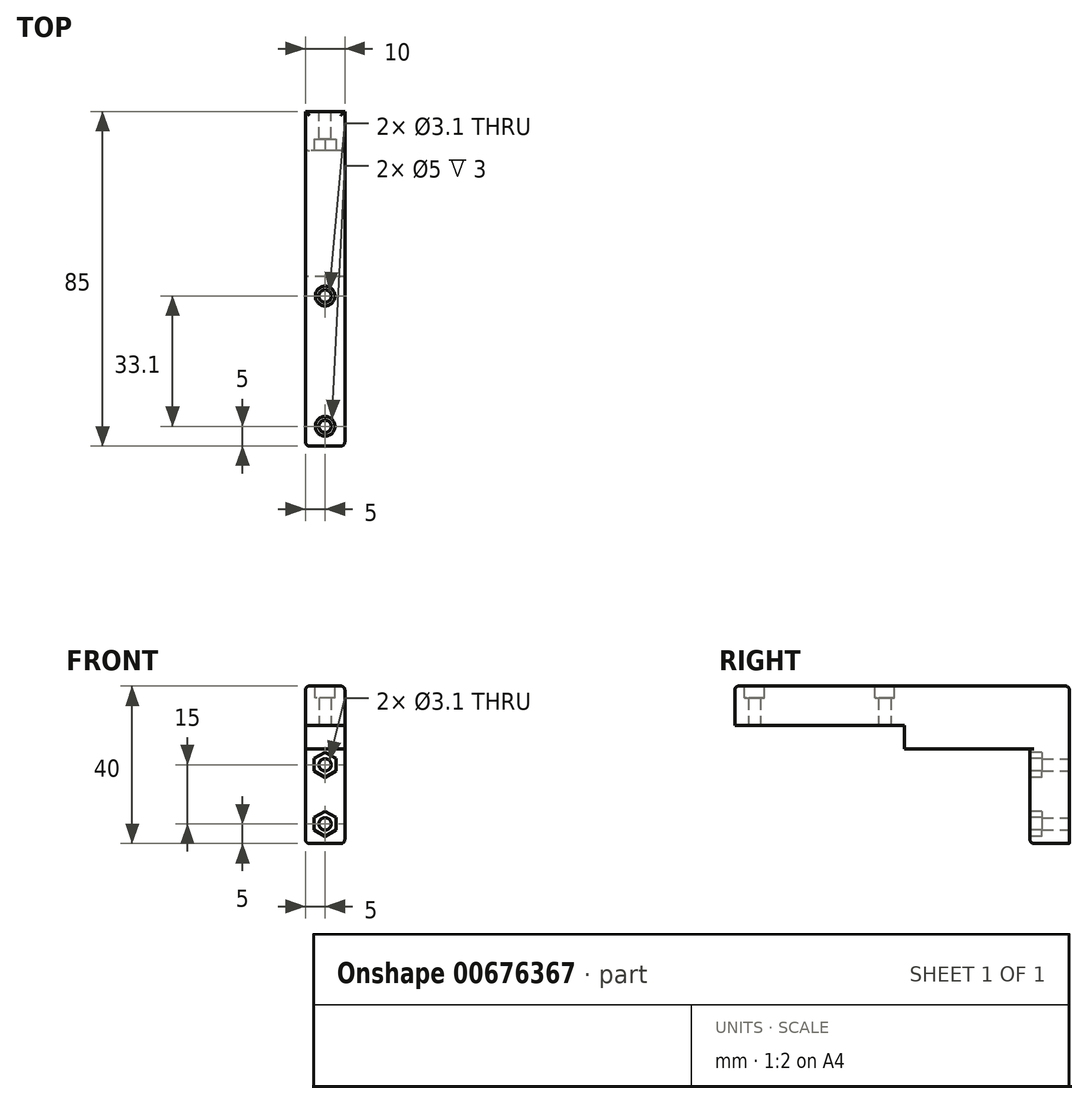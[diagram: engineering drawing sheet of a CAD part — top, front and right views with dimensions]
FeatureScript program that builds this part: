
annotation { "Feature Type Name" : "Feature", "Feature Type Description" : "" }
export const myFeature = defineFeature(function(context is Context, id is Id, definition is map)
    precondition{}
    {
        {
            var Q0;
            Q0=qCreatedBy(makeId("Top.planeOp"),FACE);
            var sketch = newSketch(context, id + "F0", { "sketchPlane" : qUnion([Q0])});
            skLineSegment(sketch, "E0.bottom", {"start": v(0, 0) * mm, "end": v(-10, 0) * mm});
            skLineSegment(sketch, "E0.top", {"start": v(0, 85) * mm, "end": v(-10, 85) * mm});
            skLineSegment(sketch, "E0.left", {"start": v(0, 0) * mm, "end": v(0, 85) * mm});
            skLineSegment(sketch, "E0.right", {"start": v(-10, 0) * mm, "end": v(-10, 85) * mm});
            skCircle(sketch, "E1", {"center": v(-5, 5) * mm, "radius": 1.55 * mm});
            skPoint(sketch, "E1.centerSnap0", {"position": v(-5, 0) * mm});
            skCircle(sketch, "E2", {"center": v(-5, 38.1) * mm, "radius": 1.55 * mm});
            skLineSegment(sketch, "E3", {"start": v(0, 43.1) * mm, "end": v(-10, 43.1) * mm});
            skLineSegment(sketch, "E4", {"start": v(0, 75) * mm, "end": v(-10, 75) * mm});
            skSolve(sketch);
        }
        {
            var Q0;
            {var subQ1=sQuery(id+"F0.wireOp",EDGE,"E0.bottom");Q0=makeQuery(id+"F0.imprint","IMPRINT",FACE,{"disambiguationData":[TD([[makeQuery(id+"F0.imprint","IMPRINT",EDGE,{"derivedFrom":subQ1}),-1.0]])]});}
            extrude(context, id + "F1", {"entities" : qUnion([Q0]), "depth" : 10 * mm, "offsetDistance" : 25 * mm});
        }
        {
            var Q0;
            {var subQ0=sQuery(id+"F0.wireOp",EDGE,"E3");Q0=makeQuery(id+"F0.imprint","IMPRINT",FACE,{"disambiguationData":[TD([[makeQuery(id+"F0.imprint","IMPRINT",EDGE,{"derivedFrom":subQ0}),-1.0]])]});}
            extrude(context, id + "F2", {"entities" : qUnion([Q0]), "operationType" : NewBodyOperationType.ADD, "depth" : 10 * mm, "offsetDistance" : 25 * mm, "hasSecondDirection" : true, "secondDirectionOppositeDirection" : true, "secondDirectionDepth" : 6 * mm});
        }
        {
            var Q0;
            {var subQ0=sQuery(id+"F0.wireOp",EDGE,"E0.top");Q0=makeQuery(id+"F0.imprint","IMPRINT",FACE,{"disambiguationData":[TD([[makeQuery(id+"F0.imprint","IMPRINT",EDGE,{"derivedFrom":subQ0}),1.0]])]});}
            extrude(context, id + "F3", {"entities" : qUnion([Q0]), "operationType" : NewBodyOperationType.ADD, "oppositeDirection" : true, "depth" : 30 * mm, "offsetDistance" : 25 * mm, "hasSecondDirection" : true, "secondDirectionOppositeDirection" : false, "secondDirectionDepth" : 10 * mm});
        }
        {
            var Q0;
            Q0=makeQuery(id+"F3.opExtrude","SWEPT_FACE",FACE,{"disambiguationData":[OSD([sQuery(id+"F0.wireOp",EDGE,"E0.top")])]});
            var sketch = newSketch(context, id + "F4", { "sketchPlane" : qUnion([Q0])});
            skCircle(sketch, "E5", {"center": v(5, -10) * mm, "radius": 1.55 * mm});
            skPoint(sketch, "E5.centerSnap0", {"position": v(5, 10) * mm});
            skPoint(sketch, "E5.perimeterSnap0", {"position": v(0, -10) * mm});
            skCircle(sketch, "E6", {"center": v(5, -25) * mm, "radius": 1.55 * mm});
            skSolve(sketch);
        }
        {
            var Q0;
            Q0=makeQuery(id+"F4.imprint","IMPRINT",FACE,{"disambiguationData":[TD([[makeQuery(id+"F4.imprint","IMPRINT",EDGE,{"derivedFrom":sQuery(id+"F4.wireOp",EDGE,"E6")}),1.0]])]});
            var Q1;
            Q1=makeQuery(id+"F4.imprint","IMPRINT",FACE,{"disambiguationData":[TD([[makeQuery(id+"F4.imprint","IMPRINT",EDGE,{"derivedFrom":sQuery(id+"F4.wireOp",EDGE,"E5")}),1.0]])]});
            extrude(context, id + "F5", {"entities" : qUnion([Q0, Q1]), "operationType" : NewBodyOperationType.REMOVE, "oppositeDirection" : true, "depth" : 15 * mm, "offsetDistance" : 25 * mm});
        }
        {
            var Q0;
            {var subQ0=sQuery(id+"F0.wireOp",EDGE,"E0.right");Q0=makeQuery(id+"F3.boolean.opBoolean","MERGE",EDGE,{"derivedFrom":[makeQuery(id+"F2.boolean.opBoolean","MERGE",EDGE,{"derivedFrom":[makeQuery(id+"F1.opExtrude","CAP_EDGE",EDGE,{"disambiguationData":[OSD([subQ0])],"isStart":false}),makeQuery(id+"F2.opExtrude","CAP_EDGE",EDGE,{"disambiguationData":[OSD([subQ0])],"isStart":false})]}),makeQuery(id+"F3.opExtrude","CAP_EDGE",EDGE,{"disambiguationData":[OSD([subQ0])],"isStart":true})]});}
            var Q1;
            {var subQ0=sQuery(id+"F0.wireOp",EDGE,"E0.left");Q1=makeQuery(id+"F3.boolean.opBoolean","MERGE",EDGE,{"derivedFrom":[makeQuery(id+"F2.boolean.opBoolean","MERGE",EDGE,{"derivedFrom":[makeQuery(id+"F1.opExtrude","CAP_EDGE",EDGE,{"disambiguationData":[OSD([subQ0])],"isStart":false}),makeQuery(id+"F2.opExtrude","CAP_EDGE",EDGE,{"disambiguationData":[OSD([subQ0])],"isStart":false})]}),makeQuery(id+"F3.opExtrude","CAP_EDGE",EDGE,{"disambiguationData":[OSD([subQ0])],"isStart":true})]});}
            var Q2;
            Q2=makeQuery(id+"F3.opExtrude","CAP_EDGE",EDGE,{"disambiguationData":[OSD([sQuery(id+"F0.wireOp",EDGE,"E0.top")])],"isStart":true});
            var Q3;
            Q3=makeQuery(id+"F3.opExtrude","SWEPT_EDGE",EDGE,{"disambiguationData":[OSD([sQuery(id+"F0.wireOp",EDGE,"E0.right"),sQuery(id+"F0.wireOp",EDGE,"E4")])]});
            var Q4;
            Q4=makeQuery(id+"F3.opExtrude","CAP_EDGE",EDGE,{"disambiguationData":[OSD([sQuery(id+"F0.wireOp",EDGE,"E4")])],"isStart":false});
            var Q5;
            Q5=makeQuery(id+"F3.opExtrude","CAP_EDGE",EDGE,{"disambiguationData":[OSD([sQuery(id+"F0.wireOp",EDGE,"E0.left")])],"isStart":false});
            var Q6;
            Q6=makeQuery(id+"F3.opExtrude","CAP_EDGE",EDGE,{"disambiguationData":[OSD([sQuery(id+"F0.wireOp",EDGE,"E0.right")])],"isStart":false});
            var Q7;
            Q7=makeQuery(id+"F1.opExtrude","SWEPT_EDGE",EDGE,{"disambiguationData":[OSD([sQuery(id+"F0.wireOp",EDGE,"E0.bottom"),sQuery(id+"F0.wireOp",EDGE,"E0.right")])]});
            var Q8;
            Q8=makeQuery(id+"F1.opExtrude","SWEPT_EDGE",EDGE,{"disambiguationData":[OSD([sQuery(id+"F0.wireOp",EDGE,"E0.bottom"),sQuery(id+"F0.wireOp",EDGE,"E0.left")])]});
            var Q9;
            Q9=makeQuery(id+"F1.opExtrude","CAP_EDGE",EDGE,{"disambiguationData":[OSD([sQuery(id+"F0.wireOp",EDGE,"E0.bottom")])],"isStart":false});
            var Q10;
            Q10=makeQuery(id+"F3.opExtrude","SWEPT_EDGE",EDGE,{"disambiguationData":[OSD([sQuery(id+"F0.wireOp",EDGE,"E0.left"),sQuery(id+"F0.wireOp",EDGE,"E4")])]});
            fillet(context, id + "F6", {"entities" : qUnion([Q0, Q1, Q2, Q3, Q4, Q5, Q6, Q7, Q8, Q9, Q10]), "radius" : 1 * mm, "tangentPropagation" : true, "allowEdgeOverflow" : false});
        }
        {
            var Q0;
            Q0=makeQuery(id+"F3.opExtrude","SWEPT_FACE",FACE,{"disambiguationData":[OSD([sQuery(id+"F0.wireOp",EDGE,"E4")])]});
            var sketch = newSketch(context, id + "F7", { "sketchPlane" : qUnion([Q0])});
            skCircle(sketch, "E7.cCircle", {"center": v(-5, -10) * mm, "radius": 2.75 * mm, "construction": true});
            skLineSegment(sketch, "E7.0", {"start": v(-2.25, -8.41) * mm, "end": v(-2.25, -11.59) * mm});
            skLineSegment(sketch, "E7.1", {"start": v(-2.25, -11.59) * mm, "end": v(-5, -13.18) * mm});
            skLineSegment(sketch, "E7.2", {"start": v(-5, -13.18) * mm, "end": v(-7.75, -11.59) * mm});
            skLineSegment(sketch, "E7.3", {"start": v(-7.75, -11.59) * mm, "end": v(-7.75, -8.41) * mm});
            skLineSegment(sketch, "E7.4", {"start": v(-7.75, -8.41) * mm, "end": v(-5, -6.82) * mm});
            skLineSegment(sketch, "E7.5", {"start": v(-5, -6.82) * mm, "end": v(-2.25, -8.41) * mm});
            skPoint(sketch, "E7.0.midPoint", {"position": v(-2.25, -10) * mm});
            skCircle(sketch, "E8.cCircle", {"center": v(-5, -25) * mm, "radius": 2.75 * mm, "construction": true});
            skLineSegment(sketch, "E8.0", {"start": v(-2.25, -23.41) * mm, "end": v(-2.25, -26.59) * mm});
            skLineSegment(sketch, "E8.1", {"start": v(-2.25, -26.59) * mm, "end": v(-5, -28.18) * mm});
            skLineSegment(sketch, "E8.2", {"start": v(-5, -28.18) * mm, "end": v(-7.75, -26.59) * mm});
            skLineSegment(sketch, "E8.3", {"start": v(-7.75, -26.59) * mm, "end": v(-7.75, -23.41) * mm});
            skLineSegment(sketch, "E8.4", {"start": v(-7.75, -23.41) * mm, "end": v(-5, -21.82) * mm});
            skLineSegment(sketch, "E8.5", {"start": v(-5, -21.82) * mm, "end": v(-2.25, -23.41) * mm});
            skPoint(sketch, "E8.0.midPoint", {"position": v(-2.25, -25) * mm});
            skSolve(sketch);
        }
        {
            var Q0;
            Q0=makeQuery(id+"F7.imprint","IMPRINT",FACE,{"disambiguationData":[TD([[makeQuery(id+"F7.imprint","IMPRINT",EDGE,{"derivedFrom":sQuery(id+"F7.wireOp",EDGE,"E7.0")}),-1.0]])]});
            var Q1;
            Q1=makeQuery(id+"F7.imprint","IMPRINT",FACE,{"disambiguationData":[TD([[makeQuery(id+"F7.imprint","IMPRINT",EDGE,{"derivedFrom":sQuery(id+"F7.wireOp",EDGE,"E8.0")}),-1.0]])]});
            extrude(context, id + "F8", {"entities" : qUnion([Q0, Q1]), "operationType" : NewBodyOperationType.REMOVE, "oppositeDirection" : true, "depth" : 3 * mm, "offsetDistance" : 25 * mm});
        }
        {
            var Q0;
            {var subQ0=sQuery(id+"F0.wireOp",EDGE,"E4");var subQ1=sQuery(id+"F0.wireOp",EDGE,"E0.right");var subQ2=sQuery(id+"F0.wireOp",EDGE,"E0.left");var subQ3=sQuery(id+"F0.wireOp",EDGE,"E3");Q0=makeQuery(id+"F3.boolean.opBoolean","MERGE",FACE,{"derivedFrom":[makeQuery(id+"F2.boolean.opBoolean","MERGE",FACE,{"derivedFrom":[makeQuery(id+"F1.opExtrude","CAP_FACE",FACE,{"disambiguationData":[OSD([sQuery(id+"F0.wireOp",EDGE,"E0.bottom"),subQ2,subQ1,sQuery(id+"F0.wireOp",EDGE,"E1"),sQuery(id+"F0.wireOp",EDGE,"E2"),subQ3])],"isStart":false}),makeQuery(id+"F2.opExtrude","CAP_FACE",FACE,{"disambiguationData":[OSD([subQ2,subQ1,subQ3,subQ0])],"isStart":false})]}),makeQuery(id+"F3.opExtrude","CAP_FACE",FACE,{"disambiguationData":[OSD([sQuery(id+"F0.wireOp",EDGE,"E0.top"),subQ2,subQ1,subQ0])],"isStart":true})]});}
            var sketch = newSketch(context, id + "F9", { "sketchPlane" : qUnion([Q0])});
            skCircle(sketch, "E9", {"center": v(-5, 38.1) * mm, "radius": 2.5 * mm});
            skCircle(sketch, "E10", {"center": v(-5, 5) * mm, "radius": 2.5 * mm});
            skSolve(sketch);
        }
        {
            var Q0;
            Q0 = qSketchRegion(id + "F9", true);
            extrude(context, id + "F10", {"entities" : qUnion([Q0]), "operationType" : NewBodyOperationType.REMOVE, "oppositeDirection" : true, "depth" : 3 * mm, "offsetDistance" : 25 * mm});
        }
    });
